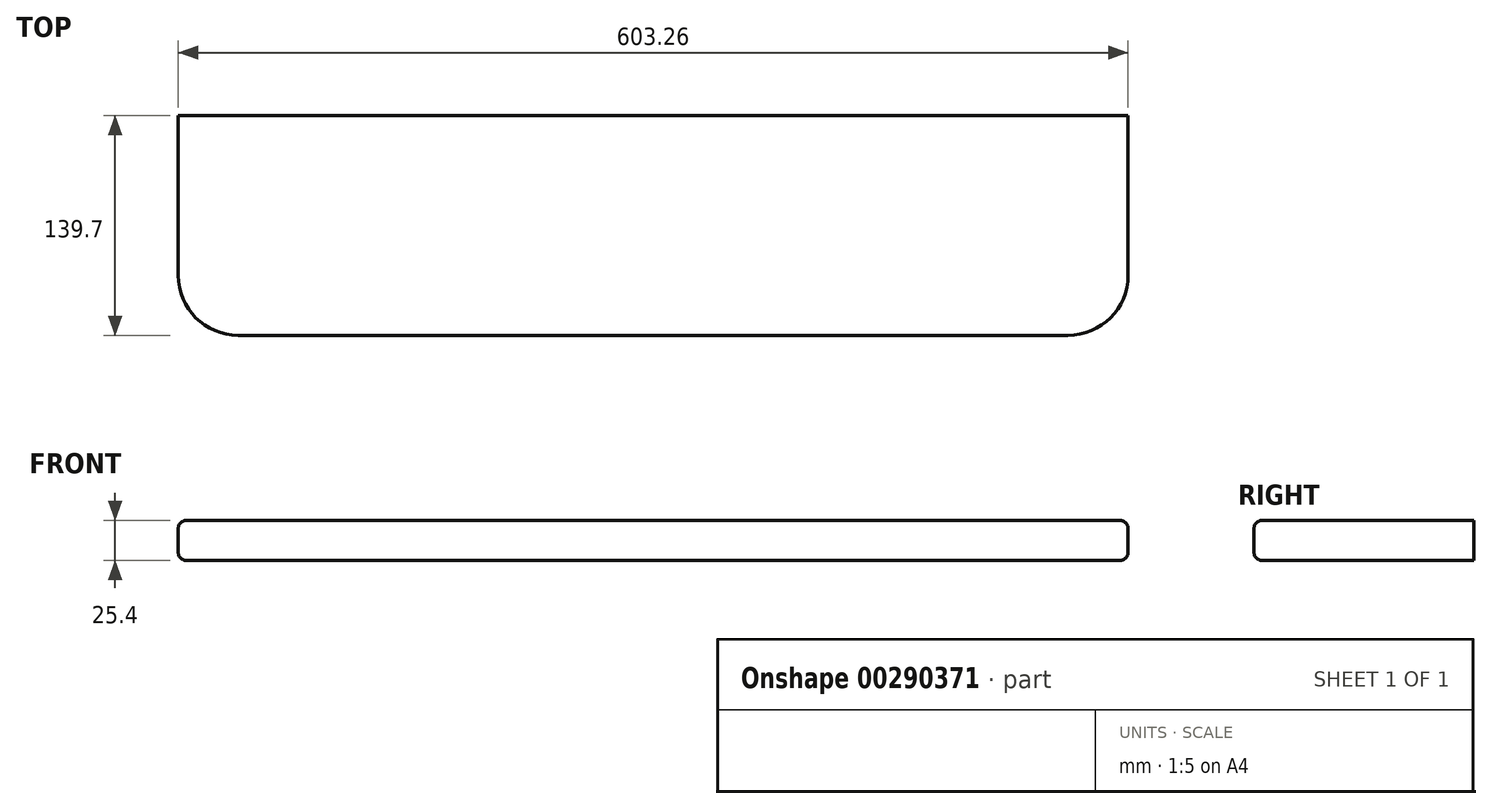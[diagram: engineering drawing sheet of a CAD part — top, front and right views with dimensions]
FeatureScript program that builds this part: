
annotation { "Feature Type Name" : "Feature", "Feature Type Description" : "" }
export const myFeature = defineFeature(function(context is Context, id is Id, definition is map)
    precondition{}
    {
        {
            var Q0;
            Q0=qCreatedBy(makeId("Top.planeOp"),FACE);
            var sketch = newSketch(context, id + "F0", { "sketchPlane" : qUnion([Q0])});
            skLineSegment(sketch, "E0.bottom", {"start": v(301.63, 69.85) * mm, "end": v(-301.63, 69.85) * mm});
            skLineSegment(sketch, "E0.top", {"start": v(263.53, -69.85) * mm, "end": v(-263.53, -69.85) * mm});
            skLineSegment(sketch, "E0.left", {"start": v(301.63, 69.85) * mm, "end": v(301.63, -31.75) * mm});
            skLineSegment(sketch, "E0.right", {"start": v(-301.63, 69.85) * mm, "end": v(-301.63, -31.75) * mm});
            skPoint(sketch, "E0.middle", {"position": v(0, 0) * mm});
            skPoint(sketch, "E1.visualSharp", {"position": v(-301.63, -69.85) * mm});
            skArc(sketch, "E1.filletArc", {"start": v(-301.63, -31.75) * mm, "mid": v(-290.47, -58.7) * mm, "end": v(-263.53, -69.85) * mm});
            skPoint(sketch, "E2.visualSharp", {"position": v(301.63, -69.85) * mm});
            skArc(sketch, "E2.filletArc", {"start": v(263.53, -69.85) * mm, "mid": v(290.47, -58.7) * mm, "end": v(301.63, -31.75) * mm});
            skSolve(sketch);
        }
        {
            var Q0;
            Q0=makeQuery(id+"F0.imprint","IMPRINT",FACE,{"disambiguationData":[TD([[makeQuery(id+"F0.imprint","IMPRINT",EDGE,{"derivedFrom":sQuery(id+"F0.wireOp",EDGE,"E0.bottom")}),1.0]])]});
            extrude(context, id + "F1", {"entities" : qUnion([Q0]), "depth" : 25.4 * mm});
        }
        {
            var Q0;
            Q0=makeQuery(id+"F1.opExtrude","CAP_EDGE",EDGE,{"disambiguationData":[OSD([sQuery(id+"F0.wireOp",EDGE,"E0.top")])],"isStart":false});
            var Q1;
            Q1=makeQuery(id+"F1.opExtrude","CAP_EDGE",EDGE,{"disambiguationData":[OSD([sQuery(id+"F0.wireOp",EDGE,"E0.left")])],"isStart":false});
            var Q2;
            Q2=makeQuery(id+"F1.opExtrude","CAP_EDGE",EDGE,{"disambiguationData":[OSD([sQuery(id+"F0.wireOp",EDGE,"E1.filletArc")])],"isStart":false});
            var Q3;
            Q3=makeQuery(id+"F1.opExtrude","CAP_EDGE",EDGE,{"disambiguationData":[OSD([sQuery(id+"F0.wireOp",EDGE,"E0.right")])],"isStart":false});
            var Q4;
            Q4=makeQuery(id+"F1.opExtrude","CAP_EDGE",EDGE,{"disambiguationData":[OSD([sQuery(id+"F0.wireOp",EDGE,"E2.filletArc")])],"isStart":false});
            fillet(context, id + "F2", {"entities" : qUnion([Q0, Q1, Q2, Q3, Q4]), "radius" : 5.08 * mm, "tangentPropagation" : true, "allowEdgeOverflow" : false});
        }
        {
            var Q0;
            Q0=makeQuery(id+"F1.opExtrude","CAP_EDGE",EDGE,{"disambiguationData":[OSD([sQuery(id+"F0.wireOp",EDGE,"E0.right")])],"isStart":true});
            var Q1;
            Q1=makeQuery(id+"F1.opExtrude","CAP_EDGE",EDGE,{"disambiguationData":[OSD([sQuery(id+"F0.wireOp",EDGE,"E1.filletArc")])],"isStart":true});
            var Q2;
            Q2=makeQuery(id+"F1.opExtrude","CAP_EDGE",EDGE,{"disambiguationData":[OSD([sQuery(id+"F0.wireOp",EDGE,"E0.top")])],"isStart":true});
            var Q3;
            Q3=makeQuery(id+"F1.opExtrude","CAP_EDGE",EDGE,{"disambiguationData":[OSD([sQuery(id+"F0.wireOp",EDGE,"E2.filletArc")])],"isStart":true});
            var Q4;
            Q4=makeQuery(id+"F1.opExtrude","CAP_EDGE",EDGE,{"disambiguationData":[OSD([sQuery(id+"F0.wireOp",EDGE,"E0.left")])],"isStart":true});
            fillet(context, id + "F3", {"entities" : qUnion([Q0, Q1, Q2, Q3, Q4]), "radius" : 5.08 * mm, "tangentPropagation" : true, "allowEdgeOverflow" : false});
        }
        {
            var Q0;
            Q0=makeQuery(id+"F1.opExtrude","CAP_FACE",FACE,{"disambiguationData":[OSD([sQuery(id+"F0.wireOp",EDGE,"E0.bottom"),sQuery(id+"F0.wireOp",EDGE,"E0.top"),sQuery(id+"F0.wireOp",EDGE,"E0.left"),sQuery(id+"F0.wireOp",EDGE,"E0.right"),sQuery(id+"F0.wireOp",EDGE,"E1.filletArc"),sQuery(id+"F0.wireOp",EDGE,"E2.filletArc")])],"isStart":false});
            var sketch = newSketch(context, id + "F4", { "sketchPlane" : qUnion([Q0])});
            skSolve(sketch);
        }
    });
